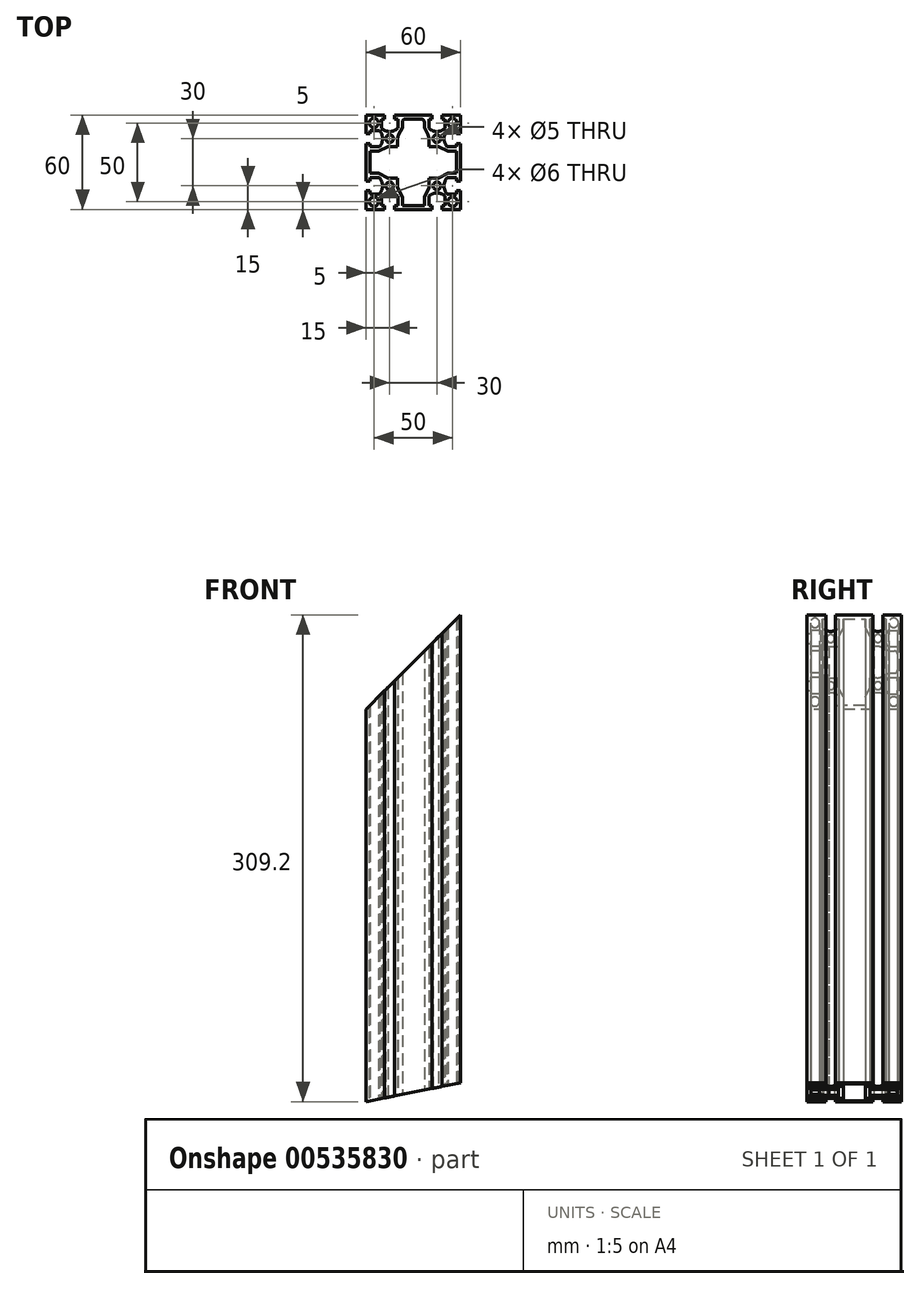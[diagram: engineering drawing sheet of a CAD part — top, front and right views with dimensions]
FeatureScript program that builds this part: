
annotation { "Feature Type Name" : "Feature", "Feature Type Description" : "" }
export const myFeature = defineFeature(function(context is Context, id is Id, definition is map)
    precondition{}
    {
        {
            var Q0;
            Q0=qCreatedBy(makeId("Top.planeOp"),FACE);
            var sketch = newSketch(context, id + "F0", { "sketchPlane" : qUnion([Q0])});
            skLineSegment(sketch, "E0.bottom", {"start": v(30, -30) * mm, "end": v(-30, -30) * mm});
            skLineSegment(sketch, "E0.top", {"start": v(30, 30) * mm, "end": v(-30, 30) * mm});
            skLineSegment(sketch, "E0.left", {"start": v(30, -30) * mm, "end": v(30, 30) * mm});
            skLineSegment(sketch, "E0.right", {"start": v(-30, -30) * mm, "end": v(-30, 30) * mm});
            skPoint(sketch, "E0.middle", {"position": v(0, 0) * mm});
            skLineSegment(sketch, "E1.top", {"start": v(-11.85, 30) * mm, "end": v(-18.15, 30) * mm});
            skLineSegment(sketch, "E1.left", {"start": v(-11.85, 27.5) * mm, "end": v(-11.85, 30) * mm});
            skLineSegment(sketch, "E1.right", {"start": v(-18.15, 27.5) * mm, "end": v(-18.15, 30) * mm});
            skPoint(sketch, "E1.middle", {"position": v(-15, 28.75) * mm});
            skLineSegment(sketch, "E2.bottom", {"start": v(-9.85, 27.5) * mm, "end": v(-11.85, 27.5) * mm});
            skLineSegment(sketch, "E2.left", {"start": v(-9.85, 27.5) * mm, "end": v(-9.85, 21.55) * mm});
            skLineSegment(sketch, "E2.right", {"start": v(-20.15, 27.5) * mm, "end": v(-20.15, 21.55) * mm});
            skPoint(sketch, "E2.middle", {"position": v(-15, 24.52) * mm});
            skArc(sketch, "E3", {"start": v(-20.15, 21.55) * mm, "mid": v(-15, 19.5) * mm, "end": v(-9.85, 21.55) * mm});
            skPoint(sketch, "E4.MirrorP", {"position": v(15, 24.52) * mm});
            skPoint(sketch, "E5.MirrorP", {"position": v(15, 28.75) * mm});
            skLineSegment(sketch, "E6.MirrorCS", {"start": v(11.85, 27.5) * mm, "end": v(11.85, 30) * mm});
            skLineSegment(sketch, "E7.MirrorCS", {"start": v(18.15, 27.5) * mm, "end": v(18.15, 30) * mm});
            skLineSegment(sketch, "E8.MirrorCS", {"start": v(9.85, 27.5) * mm, "end": v(11.85, 27.5) * mm});
            skLineSegment(sketch, "E9.MirrorCS", {"start": v(9.85, 27.5) * mm, "end": v(9.85, 21.55) * mm});
            skArc(sketch, "E10.MirrorCS", {"start": v(20.15, 21.55) * mm, "mid": v(15, 19.5) * mm, "end": v(9.85, 21.55) * mm});
            skLineSegment(sketch, "E11.MirrorCS", {"start": v(20.15, 27.5) * mm, "end": v(20.15, 21.55) * mm});
            skLineSegment(sketch, "E12.MirrorCS", {"start": v(11.85, 30) * mm, "end": v(18.15, 30) * mm});
            skLineSegment(sketch, "E13.1.0", {"start": v(27.5, 20.15) * mm, "end": v(21.55, 20.15) * mm});
            skLineSegment(sketch, "E13.1.1", {"start": v(27.5, 9.85) * mm, "end": v(21.55, 9.85) * mm});
            skArc(sketch, "E13.1.2", {"start": v(21.55, 20.15) * mm, "mid": v(19.5, 15) * mm, "end": v(21.55, 9.85) * mm});
            skLineSegment(sketch, "E13.1.3", {"start": v(27.5, -9.85) * mm, "end": v(21.55, -9.85) * mm});
            skLineSegment(sketch, "E13.1.4", {"start": v(27.5, -20.15) * mm, "end": v(21.55, -20.15) * mm});
            skPoint(sketch, "E13.1.5", {"position": v(28.75, 15) * mm});
            skPoint(sketch, "E13.1.6", {"position": v(28.75, -15) * mm});
            skArc(sketch, "E13.1.7", {"start": v(21.55, -20.15) * mm, "mid": v(19.5, -15) * mm, "end": v(21.55, -9.85) * mm});
            skPoint(sketch, "E13.1.8", {"position": v(24.52, -15) * mm});
            skPoint(sketch, "E13.1.9", {"position": v(24.52, 15) * mm});
            skLineSegment(sketch, "E13.1.10", {"start": v(27.5, 9.85) * mm, "end": v(27.5, 20.15) * mm});
            skLineSegment(sketch, "E13.1.11", {"start": v(27.5, -11.85) * mm, "end": v(27.5, -18.15) * mm});
            skLineSegment(sketch, "E13.1.12", {"start": v(30, 11.85) * mm, "end": v(30, 18.15) * mm});
            skLineSegment(sketch, "E13.1.13", {"start": v(30, -11.85) * mm, "end": v(30, -18.15) * mm});
            skLineSegment(sketch, "E13.1.14", {"start": v(27.5, 18.15) * mm, "end": v(30, 18.15) * mm});
            skLineSegment(sketch, "E13.1.15", {"start": v(27.5, 11.85) * mm, "end": v(30, 11.85) * mm});
            skLineSegment(sketch, "E13.1.16", {"start": v(27.5, 11.85) * mm, "end": v(27.5, 18.15) * mm});
            skLineSegment(sketch, "E13.1.17", {"start": v(27.5, -9.85) * mm, "end": v(27.5, -20.15) * mm});
            skLineSegment(sketch, "E13.1.18", {"start": v(27.5, -18.15) * mm, "end": v(30, -18.15) * mm});
            skLineSegment(sketch, "E13.1.19", {"start": v(27.5, -11.85) * mm, "end": v(30, -11.85) * mm});
            skLineSegment(sketch, "E13.2.0", {"start": v(20.15, -27.5) * mm, "end": v(20.15, -21.55) * mm});
            skLineSegment(sketch, "E13.2.1", {"start": v(9.85, -27.5) * mm, "end": v(9.85, -21.55) * mm});
            skArc(sketch, "E13.2.2", {"start": v(20.15, -21.55) * mm, "mid": v(15, -19.5) * mm, "end": v(9.85, -21.55) * mm});
            skLineSegment(sketch, "E13.2.3", {"start": v(-9.85, -27.5) * mm, "end": v(-9.85, -21.55) * mm});
            skLineSegment(sketch, "E13.2.4", {"start": v(-20.15, -27.5) * mm, "end": v(-20.15, -21.55) * mm});
            skPoint(sketch, "E13.2.5", {"position": v(15, -28.75) * mm});
            skPoint(sketch, "E13.2.6", {"position": v(-15, -28.75) * mm});
            skArc(sketch, "E13.2.7", {"start": v(-20.15, -21.55) * mm, "mid": v(-15, -19.5) * mm, "end": v(-9.85, -21.55) * mm});
            skPoint(sketch, "E13.2.8", {"position": v(-15, -24.52) * mm});
            skPoint(sketch, "E13.2.9", {"position": v(15, -24.52) * mm});
            skLineSegment(sketch, "E13.2.10", {"start": v(9.85, -27.5) * mm, "end": v(20.15, -27.5) * mm});
            skLineSegment(sketch, "E13.2.11", {"start": v(-11.85, -27.5) * mm, "end": v(-18.15, -27.5) * mm});
            skLineSegment(sketch, "E13.2.12", {"start": v(11.85, -30) * mm, "end": v(18.15, -30) * mm});
            skLineSegment(sketch, "E13.2.13", {"start": v(-11.85, -30) * mm, "end": v(-18.15, -30) * mm});
            skLineSegment(sketch, "E13.2.14", {"start": v(18.15, -27.5) * mm, "end": v(18.15, -30) * mm});
            skLineSegment(sketch, "E13.2.15", {"start": v(11.85, -27.5) * mm, "end": v(11.85, -30) * mm});
            skLineSegment(sketch, "E13.2.16", {"start": v(11.85, -27.5) * mm, "end": v(18.15, -27.5) * mm});
            skLineSegment(sketch, "E13.2.17", {"start": v(-9.85, -27.5) * mm, "end": v(-20.15, -27.5) * mm});
            skLineSegment(sketch, "E13.2.18", {"start": v(-18.15, -27.5) * mm, "end": v(-18.15, -30) * mm});
            skLineSegment(sketch, "E13.2.19", {"start": v(-11.85, -27.5) * mm, "end": v(-11.85, -30) * mm});
            skLineSegment(sketch, "E13.3.0", {"start": v(-27.5, -20.15) * mm, "end": v(-21.55, -20.15) * mm});
            skLineSegment(sketch, "E13.3.1", {"start": v(-27.5, -9.85) * mm, "end": v(-21.55, -9.85) * mm});
            skArc(sketch, "E13.3.2", {"start": v(-21.55, -20.15) * mm, "mid": v(-19.5, -15) * mm, "end": v(-21.55, -9.85) * mm});
            skLineSegment(sketch, "E13.3.3", {"start": v(-27.5, 9.85) * mm, "end": v(-21.55, 9.85) * mm});
            skLineSegment(sketch, "E13.3.4", {"start": v(-27.5, 20.15) * mm, "end": v(-21.55, 20.15) * mm});
            skPoint(sketch, "E13.3.5", {"position": v(-28.75, -15) * mm});
            skPoint(sketch, "E13.3.6", {"position": v(-28.75, 15) * mm});
            skArc(sketch, "E13.3.7", {"start": v(-21.55, 20.15) * mm, "mid": v(-19.5, 15) * mm, "end": v(-21.55, 9.85) * mm});
            skPoint(sketch, "E13.3.8", {"position": v(-24.52, 15) * mm});
            skPoint(sketch, "E13.3.9", {"position": v(-24.52, -15) * mm});
            skLineSegment(sketch, "E13.3.10", {"start": v(-27.5, -9.85) * mm, "end": v(-27.5, -20.15) * mm});
            skLineSegment(sketch, "E13.3.11", {"start": v(-27.5, 11.85) * mm, "end": v(-27.5, 18.15) * mm});
            skLineSegment(sketch, "E13.3.12", {"start": v(-30, -11.85) * mm, "end": v(-30, -18.15) * mm});
            skLineSegment(sketch, "E13.3.13", {"start": v(-30, 11.85) * mm, "end": v(-30, 18.15) * mm});
            skLineSegment(sketch, "E13.3.14", {"start": v(-27.5, -18.15) * mm, "end": v(-30, -18.15) * mm});
            skLineSegment(sketch, "E13.3.15", {"start": v(-27.5, -11.85) * mm, "end": v(-30, -11.85) * mm});
            skLineSegment(sketch, "E13.3.16", {"start": v(-27.5, -11.85) * mm, "end": v(-27.5, -18.15) * mm});
            skLineSegment(sketch, "E13.3.17", {"start": v(-27.5, 9.85) * mm, "end": v(-27.5, 20.15) * mm});
            skLineSegment(sketch, "E13.3.18", {"start": v(-27.5, 18.15) * mm, "end": v(-30, 18.15) * mm});
            skLineSegment(sketch, "E13.3.19", {"start": v(-27.5, 11.85) * mm, "end": v(-30, 11.85) * mm});
            skLineSegment(sketch, "E13.anchor1", {"start": v(0, 0) * mm, "end": v(-20.15, 21.55) * mm, "construction": true});
            skLineSegment(sketch, "E13.anchor2", {"start": v(0, 0) * mm, "end": v(-21.55, -20.15) * mm, "construction": true});
            skLineSegment(sketch, "E14.trimOffspring", {"start": v(-18.15, 27.5) * mm, "end": v(-20.15, 27.5) * mm});
            skLineSegment(sketch, "E15.trimOffspring", {"start": v(18.15, 27.5) * mm, "end": v(20.15, 27.5) * mm});
            skCircle(sketch, "E16", {"center": v(-15, 15) * mm, "radius": 2.5 * mm});
            skCircle(sketch, "E17", {"center": v(-25, 25) * mm, "radius": 3 * mm});
            skCircle(sketch, "E18.MirrorC", {"center": v(25, 25) * mm, "radius": 3 * mm});
            skCircle(sketch, "E19.MirrorC", {"center": v(25, -25) * mm, "radius": 3 * mm});
            skCircle(sketch, "E20.MirrorC", {"center": v(-25, -25) * mm, "radius": 3 * mm});
            skCircle(sketch, "E21.MirrorC", {"center": v(15, 15) * mm, "radius": 2.5 * mm});
            skCircle(sketch, "E22.MirrorC", {"center": v(15, -15) * mm, "radius": 2.5 * mm});
            skCircle(sketch, "E23.MirrorC", {"center": v(-15, -15) * mm, "radius": 2.5 * mm});
            skLineSegment(sketch, "E24", {"start": v(-7, 27.5) * mm, "end": v(0, 27.5) * mm});
            skLineSegment(sketch, "E25", {"start": v(-7, 27.5) * mm, "end": v(-7, 22) * mm});
            skLineSegment(sketch, "E26", {"start": v(-10, 10) * mm, "end": v(-10, 16) * mm});
            skLineSegment(sketch, "E27", {"start": v(-10, 16) * mm, "end": v(-7, 22) * mm});
            skLineSegment(sketch, "E28.MirrorCS", {"start": v(10, 10) * mm, "end": v(10, 16) * mm});
            skLineSegment(sketch, "E29.MirrorCS", {"start": v(10, 16) * mm, "end": v(7, 22) * mm});
            skLineSegment(sketch, "E30.MirrorCS", {"start": v(7, 27.5) * mm, "end": v(0, 27.5) * mm});
            skLineSegment(sketch, "E31.MirrorCS", {"start": v(7, 27.5) * mm, "end": v(7, 22) * mm});
            skLineSegment(sketch, "E32.1.0", {"start": v(-10, -10) * mm, "end": v(-16, -10) * mm});
            skLineSegment(sketch, "E32.1.1", {"start": v(-16, -10) * mm, "end": v(-22, -7) * mm});
            skLineSegment(sketch, "E32.1.2", {"start": v(-27.5, -7) * mm, "end": v(-22, -7) * mm});
            skLineSegment(sketch, "E32.1.3", {"start": v(-27.5, -7) * mm, "end": v(-27.5, 0) * mm});
            skLineSegment(sketch, "E32.1.4", {"start": v(-27.5, 7) * mm, "end": v(-27.5, 0) * mm});
            skLineSegment(sketch, "E32.1.5", {"start": v(-27.5, 7) * mm, "end": v(-22, 7) * mm});
            skLineSegment(sketch, "E32.1.6", {"start": v(-16, 10) * mm, "end": v(-22, 7) * mm});
            skLineSegment(sketch, "E32.1.7", {"start": v(-10, 10) * mm, "end": v(-16, 10) * mm});
            skLineSegment(sketch, "E32.2.0", {"start": v(10, -10) * mm, "end": v(10, -16) * mm});
            skLineSegment(sketch, "E32.2.1", {"start": v(10, -16) * mm, "end": v(7, -22) * mm});
            skLineSegment(sketch, "E32.2.2", {"start": v(7, -27.5) * mm, "end": v(7, -22) * mm});
            skLineSegment(sketch, "E32.2.3", {"start": v(7, -27.5) * mm, "end": v(0, -27.5) * mm});
            skLineSegment(sketch, "E32.2.4", {"start": v(-7, -27.5) * mm, "end": v(0, -27.5) * mm});
            skLineSegment(sketch, "E32.2.5", {"start": v(-7, -27.5) * mm, "end": v(-7, -22) * mm});
            skLineSegment(sketch, "E32.2.6", {"start": v(-10, -16) * mm, "end": v(-7, -22) * mm});
            skLineSegment(sketch, "E32.2.7", {"start": v(-10, -10) * mm, "end": v(-10, -16) * mm});
            skLineSegment(sketch, "E32.3.0", {"start": v(10, 10) * mm, "end": v(16, 10) * mm});
            skLineSegment(sketch, "E32.3.1", {"start": v(16, 10) * mm, "end": v(22, 7) * mm});
            skLineSegment(sketch, "E32.3.2", {"start": v(27.5, 7) * mm, "end": v(22, 7) * mm});
            skLineSegment(sketch, "E32.3.3", {"start": v(27.5, 7) * mm, "end": v(27.5, 0) * mm});
            skLineSegment(sketch, "E32.3.4", {"start": v(27.5, -7) * mm, "end": v(27.5, 0) * mm});
            skLineSegment(sketch, "E32.3.5", {"start": v(27.5, -7) * mm, "end": v(22, -7) * mm});
            skLineSegment(sketch, "E32.3.6", {"start": v(16, -10) * mm, "end": v(22, -7) * mm});
            skLineSegment(sketch, "E32.3.7", {"start": v(10, -10) * mm, "end": v(16, -10) * mm});
            skSolve(sketch);
        }
        {
            var Q0;
            {var subQ30=sQuery(id+"F0.wireOp",EDGE,"E1.left");Q0=makeQuery(id+"F0.imprint","IMPRINT",FACE,{"disambiguationData":[TD([[makeQuery(id+"F0.imprint","IMPRINT",EDGE,{"derivedFrom":subQ30}),-1.0]])]});}
            extrude(context, id + "F1", {"entities" : qUnion([Q0]), "depth" : 309.2 * mm, "offsetDistance" : 25 * mm});
        }
        {
            var Q0;
            Q0=makeQuery(id+"F1.opExtrude","SWEPT_EDGE",EDGE,{"disambiguationData":[OSD([sQuery(id+"F0.wireOp",EDGE,"E24"),sQuery(id+"F0.wireOp",EDGE,"E25")])]});
            var Q1;
            Q1=makeQuery(id+"F1.opExtrude","SWEPT_EDGE",EDGE,{"disambiguationData":[OSD([sQuery(id+"F0.wireOp",EDGE,"E30.MirrorCS"),sQuery(id+"F0.wireOp",EDGE,"E31.MirrorCS")])]});
            var Q2;
            Q2=makeQuery(id+"F1.opExtrude","SWEPT_EDGE",EDGE,{"disambiguationData":[OSD([sQuery(id+"F0.wireOp",EDGE,"840db5bc-c403-45cd-90c7-254e62d9e8c5.3.2"),sQuery(id+"F0.wireOp",EDGE,"840db5bc-c403-45cd-90c7-254e62d9e8c5.3.3")])]});
            var Q3;
            Q3=makeQuery(id+"F1.opExtrude","SWEPT_EDGE",EDGE,{"disambiguationData":[OSD([sQuery(id+"F0.wireOp",EDGE,"840db5bc-c403-45cd-90c7-254e62d9e8c5.3.4"),sQuery(id+"F0.wireOp",EDGE,"840db5bc-c403-45cd-90c7-254e62d9e8c5.3.5")])]});
            var Q4;
            Q4=makeQuery(id+"F1.opExtrude","SWEPT_EDGE",EDGE,{"disambiguationData":[OSD([sQuery(id+"F0.wireOp",EDGE,"840db5bc-c403-45cd-90c7-254e62d9e8c5.1.4"),sQuery(id+"F0.wireOp",EDGE,"840db5bc-c403-45cd-90c7-254e62d9e8c5.1.5")])]});
            var Q5;
            Q5=makeQuery(id+"F1.opExtrude","SWEPT_EDGE",EDGE,{"disambiguationData":[OSD([sQuery(id+"F0.wireOp",EDGE,"840db5bc-c403-45cd-90c7-254e62d9e8c5.1.2"),sQuery(id+"F0.wireOp",EDGE,"840db5bc-c403-45cd-90c7-254e62d9e8c5.1.3")])]});
            var Q6;
            Q6=makeQuery(id+"F1.opExtrude","SWEPT_EDGE",EDGE,{"disambiguationData":[OSD([sQuery(id+"F0.wireOp",EDGE,"840db5bc-c403-45cd-90c7-254e62d9e8c5.2.2"),sQuery(id+"F0.wireOp",EDGE,"840db5bc-c403-45cd-90c7-254e62d9e8c5.2.3")])]});
            var Q7;
            Q7=makeQuery(id+"F1.opExtrude","SWEPT_EDGE",EDGE,{"disambiguationData":[OSD([sQuery(id+"F0.wireOp",EDGE,"840db5bc-c403-45cd-90c7-254e62d9e8c5.2.4"),sQuery(id+"F0.wireOp",EDGE,"840db5bc-c403-45cd-90c7-254e62d9e8c5.2.5")])]});
            fillet(context, id + "F2", {"entities" : qUnion([Q0, Q1, Q2, Q3, Q4, Q5, Q6, Q7]), "radius" : 2 * mm, "tangentPropagation" : true, "allowEdgeOverflow" : false});
        }
        {
            var Q0;
            Q0=makeQuery(id+"F1.opExtrude","SWEPT_EDGE",EDGE,{"disambiguationData":[OSD([sQuery(id+"F0.wireOp",EDGE,"E26"),sQuery(id+"F0.wireOp",EDGE,"E27")])]});
            var Q1;
            Q1=makeQuery(id+"F1.opExtrude","SWEPT_EDGE",EDGE,{"disambiguationData":[OSD([sQuery(id+"F0.wireOp",EDGE,"E28.MirrorCS"),sQuery(id+"F0.wireOp",EDGE,"E29.MirrorCS")])]});
            var Q2;
            Q2=makeQuery(id+"F1.opExtrude","SWEPT_EDGE",EDGE,{"disambiguationData":[OSD([sQuery(id+"F0.wireOp",EDGE,"840db5bc-c403-45cd-90c7-254e62d9e8c5.3.0"),sQuery(id+"F0.wireOp",EDGE,"840db5bc-c403-45cd-90c7-254e62d9e8c5.3.1")])]});
            var Q3;
            Q3=makeQuery(id+"F1.opExtrude","SWEPT_EDGE",EDGE,{"disambiguationData":[OSD([sQuery(id+"F0.wireOp",EDGE,"840db5bc-c403-45cd-90c7-254e62d9e8c5.1.6"),sQuery(id+"F0.wireOp",EDGE,"840db5bc-c403-45cd-90c7-254e62d9e8c5.1.7")])]});
            var Q4;
            Q4=makeQuery(id+"F1.opExtrude","SWEPT_EDGE",EDGE,{"disambiguationData":[OSD([sQuery(id+"F0.wireOp",EDGE,"840db5bc-c403-45cd-90c7-254e62d9e8c5.1.0"),sQuery(id+"F0.wireOp",EDGE,"840db5bc-c403-45cd-90c7-254e62d9e8c5.1.1")])]});
            var Q5;
            Q5=makeQuery(id+"F1.opExtrude","SWEPT_EDGE",EDGE,{"disambiguationData":[OSD([sQuery(id+"F0.wireOp",EDGE,"840db5bc-c403-45cd-90c7-254e62d9e8c5.3.6"),sQuery(id+"F0.wireOp",EDGE,"840db5bc-c403-45cd-90c7-254e62d9e8c5.3.7")])]});
            var Q6;
            Q6=makeQuery(id+"F1.opExtrude","SWEPT_EDGE",EDGE,{"disambiguationData":[OSD([sQuery(id+"F0.wireOp",EDGE,"840db5bc-c403-45cd-90c7-254e62d9e8c5.2.0"),sQuery(id+"F0.wireOp",EDGE,"840db5bc-c403-45cd-90c7-254e62d9e8c5.2.1")])]});
            var Q7;
            Q7=makeQuery(id+"F1.opExtrude","SWEPT_EDGE",EDGE,{"disambiguationData":[OSD([sQuery(id+"F0.wireOp",EDGE,"840db5bc-c403-45cd-90c7-254e62d9e8c5.2.6"),sQuery(id+"F0.wireOp",EDGE,"840db5bc-c403-45cd-90c7-254e62d9e8c5.2.7")])]});
            fillet(context, id + "F3", {"entities" : qUnion([Q0, Q1, Q2, Q3, Q4, Q5, Q6, Q7]), "radius" : 7 * mm, "tangentPropagation" : true, "allowEdgeOverflow" : false});
        }
        {
            var Q0;
            {var subQ0=sQuery(id+"F0.wireOp",EDGE,"E0.bottom");Q0=makeQuery(id+"F1.opExtrude","SWEPT_FACE",FACE,{"disambiguationData":[OSD([subQ0]),TDD([makeQuery(id+"F0.imprint","IMPRINT",EDGE,{"disambiguationData":[TD([[makeQuery(id+"F0.imprint","INTERSECT",VERTEX,{"derivedFrom":[subQ0,sQuery(id+"F0.wireOp",EDGE,"E13.2.12"),sQuery(id+"F0.wireOp",EDGE,"E13.2.15")]}),-1.0]])],"derivedFrom":subQ0})])]});}
            var sketch = newSketch(context, id + "F4", { "sketchPlane" : qUnion([Q0])});
            skLineSegment(sketch, "E33.0", {"start": v(-18.15, 309.2) * mm, "end": v(-30, 309.2) * mm});
            skLineSegment(sketch, "E33.1", {"start": v(30, 309.2) * mm, "end": v(30, 0) * mm});
            skLineSegment(sketch, "E34", {"start": v(-30, 309.2) * mm, "end": v(30, 309.2) * mm});
            skLineSegment(sketch, "E35", {"start": v(30, 249.2) * mm, "end": v(-30, 309.2) * mm});
            skLineSegment(sketch, "E36.0", {"start": v(-18.15, 0) * mm, "end": v(-30, 0) * mm});
            skLineSegment(sketch, "E37", {"start": v(-30, 0) * mm, "end": v(30, 0) * mm});
            skLineSegment(sketch, "E38", {"start": v(30, 60) * mm, "end": v(-30, 0) * mm});
            skSolve(sketch);
        }
        {
            var Q0;
            Q0=qCreatedBy(makeId("Front.planeOp"),FACE);
            var sketch = newSketch(context, id + "F5", { "sketchPlane" : qUnion([Q0])});
            skLineSegment(sketch, "E39.bottom", {"start": v(175.88, 40.95) * mm, "end": v(-30, 0) * mm});
            skLineSegment(sketch, "E39.top", {"start": v(199.67, -78.65) * mm, "end": v(-6.2, -119.6) * mm});
            skLineSegment(sketch, "E39.left", {"start": v(175.88, 40.95) * mm, "end": v(199.67, -78.65) * mm});
            skLineSegment(sketch, "E39.right", {"start": v(-30, 0) * mm, "end": v(-6.2, -119.6) * mm});
            skLineSegment(sketch, "E40.bottom", {"start": v(-52.07, 391.27) * mm, "end": v(-206.7, 236.66) * mm});
            skLineSegment(sketch, "E40.top", {"start": v(30, 309.2) * mm, "end": v(-124.62, 154.58) * mm});
            skLineSegment(sketch, "E40.left", {"start": v(-52.07, 391.27) * mm, "end": v(30, 309.2) * mm});
            skLineSegment(sketch, "E40.right", {"start": v(-206.7, 236.66) * mm, "end": v(-124.62, 154.58) * mm});
            skSolve(sketch);
        }
        {
            var Q0;
            Q0 = qSketchRegion(id + "F5", true);
            extrude(context, id + "F6", {"entities" : qUnion([Q0]), "operationType" : NewBodyOperationType.REMOVE, "depth" : 30 * mm, "offsetDistance" : 25 * mm, "hasSecondDirection" : true, "secondDirectionOppositeDirection" : true, "secondDirectionDepth" : 30 * mm});
        }
    });
